# Revit family: IS_Eurovit_V3122_BIM_NL
name_source: partatom
category: Plumbing Fixtures
revit_build: Autodesk Revit MEP 2014 (Build: 20130308_1515(x64)
units: mm (PartAtom-declared; Revit-internal decimal feet)

## types (1)
- V312201 - EUROVIT STAAND CLOSET DIEPSPOEL PK
    Accessories = www.idealstandardnederland.nl
    AreaUnits = millimeters
    Assembly Code = C1030200
    AssetType = Vast
    BIMObjectName = ISI_IdealStandard_WcPans_V312201
    BREEAMApproved = No
    BarCode = 8595095932845
    Brand = Ideal Standard
    CWFU = 0
    CodePerformance = DIN EN 997 CL1-6AC, DIN EN 33
    ConnectionType = Sanitair
    Cost = 0 $
    Default Elevation = 0 mm  [stored 0 ft]
    Description = Eurovit staand closet diepspoel van keramiek. DIN EN 997. Geglazuurde spoelrand. Uitgang H/PK (horizontaal). Voor opbouw- of inbouwreservoir met 6 liter spoeling of opbouw of inbouw drukspoelers G3/4". Bevestiging met 2 schroeven M6 x 70 mm (K711067). Exclusief closetzitting.
    DurationUnit = jaar
    ECA = No
    ExpectedLife = 25
    Features = Staand closet diepspoel van keramiek. DIN EN 997. Geglazuurde spoelrand. Uitgang H/PK (horizontaal). Voor opbouw- of inbouwreservoir met 6 liter spoeling of opbouw of inbouw drukspoelers G3/4". Bevestiging met 2 schroeven M6 x 70 mm (K711067). Exclusief closetzitting.
    Finish = Wit
    HWFU = 0
    IfcExportAs = IfcSanitaryTerminalType
    IfcExportType = TOILETPAN
    InstallationInstructions = http://www.idealstandardnederland.nl
    LinearUnits = millimeters
    ManufacturerURL = www.idealstandardnederland.nl
    Model = V312201
    ModelNumber = V312201
    ModelReference = Eurovit staand closet diepspoel van keramiek. DIN EN 997. Geglazuurde spoelrand. Uitgang H/PK (horizontaal). Voor opbouw- of inbouwreservoir met 6 liter spoeling of opbouw of inbouw drukspoelers G3/4". Bevestiging met 2 schroeven M6 x 70 mm (K711067). Exclusief closetzitting.
    NBSDescription = WC pans
    NBSReference = 45-30-70/384
    Name = WcPans_V312201_IdealStandard
    NettWeight = 14.07 kg
    NominalDepth = 0 mm  [stored 0 ft]
    NominalHeight = 390 mm
    NominalLength = 480 mm
    NominalWidth = 355 mm
    PanColor = Wit
    PanMaterial = Keramiek
    PanMounting = BackToWall
    ProductInformation = http://www.idealstandardnederland.nl
    Shape = Gesculptuurd
    Size = 355 x 480 x 390 mm
    Space = Internal
    SpilloverLevel = 0 mm  [stored 0 ft]
    ToiletPanType = WashDown
    ToiletType = Other
    URL = www.idealstandardnederland.nl
    Uniclass2015Code = Pr_40_20_93_94
    Uniclass2015Title = WC pans
    Uniclass2015Version = Products v1.1
    Version = 1
    VolumeUnits = liter
    WFU = 0
    WRAS = No
    WarrantyDescription = Fabrieksgarantie
    WarrantyDurationParts = 5
    WarrantyDurationUnit = jaar
    WaterEfficientProduct = No

note: [stored X ft] marks values corroborated as IEEE doubles in the binary element streams (Revit-internal decimal feet)

## geometry (parser evidence)
native form markers: Sweep x2
no freeform markers — native parametric forms only
